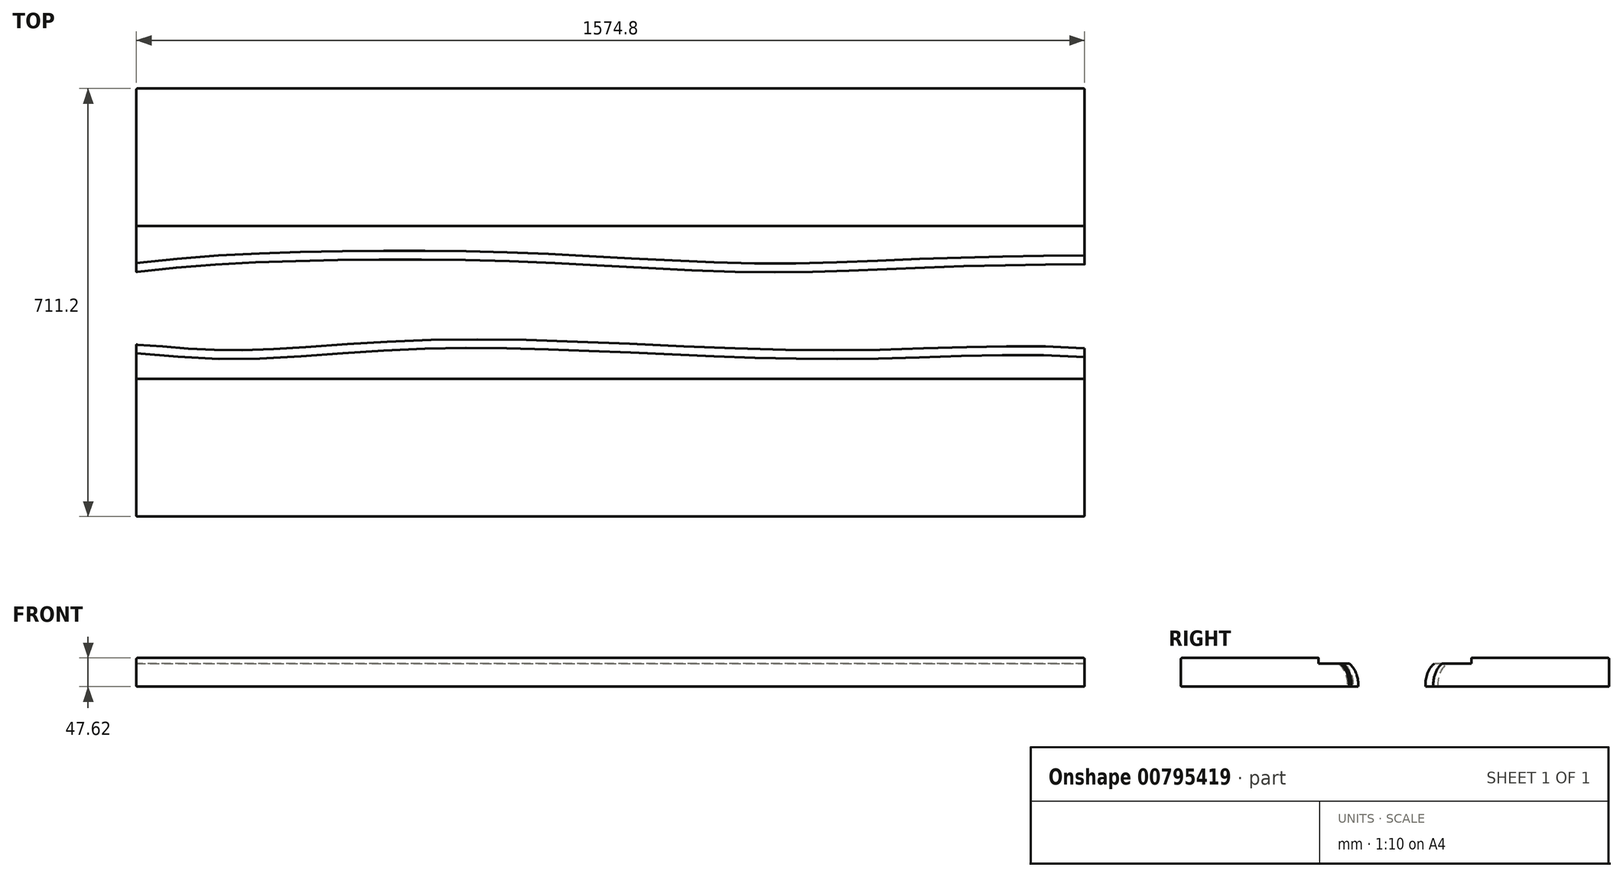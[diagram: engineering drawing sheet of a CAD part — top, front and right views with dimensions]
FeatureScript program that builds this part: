
annotation { "Feature Type Name" : "Feature", "Feature Type Description" : "" }
export const myFeature = defineFeature(function(context is Context, id is Id, definition is map)
    precondition{}
    {
        {
            var Q0;
            Q0=qCreatedBy(makeId("Top.planeOp"),FACE);
            var sketch = newSketch(context, id + "F0", { "sketchPlane" : qUnion([Q0])});
            skLineSegment(sketch, "E0.bottom", {"start": v(787.4, 355.6) * mm, "end": v(-787.4, 355.6) * mm});
            skLineSegment(sketch, "E0.top", {"start": v(787.4, -355.6) * mm, "end": v(-787.4, -355.6) * mm});
            skLineSegment(sketch, "E0.left", {"start": v(787.4, 355.6) * mm, "end": v(787.4, 63.5) * mm});
            skLineSegment(sketch, "E0.right", {"start": v(-787.4, 355.6) * mm, "end": v(-787.4, 50.8) * mm});
            skPoint(sketch, "E0.middle", {"position": v(0, 0) * mm});
            skFitSpline(sketch, "E1", {"points": [v(-787.4, 50.8) * mm, v(-491.45, 69.85) * mm, v(-145.69, 67.95) * mm, v(228.67, 50.8) * mm, v(493.84, 57.15) * mm, v(787.4, 63.5) * mm], "startDerivative": vector(1515.69, 196.01) * mm, "endDerivative": vector(1515.4, 0) * mm});
            skFitSpline(sketch, "E2", {"points": [v(-787.4, -69.85) * mm, v(-621.43, -79.38) * mm, v(-267.87, -61.35) * mm, v(361.25, -79.38) * mm, v(787.4, -76.2) * mm], "startDerivative": vector(997.51, -57.2) * mm, "endDerivative": vector(1451.8, -114.04) * mm});
            skLineSegment(sketch, "E3.trimOffspring", {"start": v(-787.4, -69.85) * mm, "end": v(-787.4, -355.6) * mm});
            skLineSegment(sketch, "E4.trimOffspring", {"start": v(787.4, -76.2) * mm, "end": v(787.4, -355.6) * mm});
            skSolve(sketch);
        }
        {
            var Q0;
            Q0 = qSketchRegion(id + "F0", true);
            extrude(context, id + "F1", {"entities" : qUnion([Q0]), "depth" : 47.62 * mm, "offsetDistance" : 25.4 * mm});
        }
        {
            var Q0;
            Q0=makeQuery(id+"F1.opExtrude","CAP_EDGE",EDGE,{"disambiguationData":[OSD([sQuery(id+"F0.wireOp",EDGE,"E2")])],"isStart":false});
            var Q1;
            Q1=makeQuery(id+"F1.opExtrude","CAP_EDGE",EDGE,{"disambiguationData":[OSD([sQuery(id+"F0.wireOp",EDGE,"E1")])],"isStart":false});
            fillet(context, id + "F2", {"entities" : qUnion([Q0, Q1]), "tangentPropagation" : true, "crossSection" : FilletCrossSection.CURVATURE, "radius" : 47.62 * mm, "magnitude" : 0.5, "defaultsChanged" : true, "vertexSettings" : []});
        }
        {
            var Q0;
            Q0=qCreatedBy(makeId("Right.planeOp"),FACE);
            var sketch = newSketch(context, id + "F3", { "sketchPlane" : qUnion([Q0])});
            skLineSegment(sketch, "E5.bottom", {"start": v(127, 38.1) * mm, "end": v(-127, 38.1) * mm});
            skLineSegment(sketch, "E5.top", {"start": v(127, 114.3) * mm, "end": v(-127, 114.3) * mm});
            skLineSegment(sketch, "E5.left", {"start": v(127, 38.1) * mm, "end": v(127, 114.3) * mm});
            skLineSegment(sketch, "E5.right", {"start": v(-127, 38.1) * mm, "end": v(-127, 114.3) * mm});
            skPoint(sketch, "E5.middle", {"position": v(0, 76.2) * mm});
            skSolve(sketch);
        }
        {
            var Q0;
            Q0 = qSketchRegion(id + "F3", true);
            extrude(context, id + "F4", {"entities" : qUnion([Q0]), "operationType" : NewBodyOperationType.REMOVE, "endBound" : BoundingType.THROUGH_ALL, "oppositeDirection" : true, "depth" : 25.4 * mm, "offsetDistance" : 25.4 * mm, "hasSecondDirection" : true, "secondDirectionBound" : SecondDirectionBoundingType.THROUGH_ALL, "secondDirectionOppositeDirection" : false, "secondDirectionDepth" : 25.4 * mm});
        }
        {
            var Q0;
            Q0=makeQuery(id+"F1.opExtrude","CAP_EDGE",EDGE,{"disambiguationData":[OSD([sQuery(id+"F0.wireOp",EDGE,"E0.right")])],"isStart":false});
            var Q1;
            Q1=makeQuery(id+"F1.opExtrude","CAP_EDGE",EDGE,{"disambiguationData":[OSD([sQuery(id+"F0.wireOp",EDGE,"E0.bottom")])],"isStart":false});
            var Q2;
            Q2=makeQuery(id+"F1.opExtrude","CAP_EDGE",EDGE,{"disambiguationData":[OSD([sQuery(id+"F0.wireOp",EDGE,"E3.trimOffspring")])],"isStart":false});
            var Q3;
            Q3=makeQuery(id+"F1.opExtrude","CAP_EDGE",EDGE,{"disambiguationData":[OSD([sQuery(id+"F0.wireOp",EDGE,"E0.top")])],"isStart":false});
            var Q4;
            Q4=makeQuery(id+"F1.opExtrude","CAP_EDGE",EDGE,{"disambiguationData":[OSD([sQuery(id+"F0.wireOp",EDGE,"E4.trimOffspring")])],"isStart":false});
            var Q5;
            Q5=makeQuery(id+"F1.opExtrude","CAP_EDGE",EDGE,{"disambiguationData":[OSD([sQuery(id+"F0.wireOp",EDGE,"E0.left")])],"isStart":false});
            var Q6;
            Q6=makeQuery(id+"F1.opExtrude","CAP_EDGE",EDGE,{"disambiguationData":[OSD([sQuery(id+"F0.wireOp",EDGE,"E0.left")])],"isStart":true});
            var Q7;
            Q7=makeQuery(id+"F1.opExtrude","CAP_EDGE",EDGE,{"disambiguationData":[OSD([sQuery(id+"F0.wireOp",EDGE,"E4.trimOffspring")])],"isStart":true});
            var Q8;
            Q8=makeQuery(id+"F1.opExtrude","CAP_EDGE",EDGE,{"disambiguationData":[OSD([sQuery(id+"F0.wireOp",EDGE,"E0.top")])],"isStart":true});
            var Q9;
            Q9=makeQuery(id+"F1.opExtrude","SWEPT_EDGE",EDGE,{"disambiguationData":[OSD([sQuery(id+"F0.wireOp",EDGE,"E0.top"),sQuery(id+"F0.wireOp",EDGE,"E4.trimOffspring")])]});
            var Q10;
            Q10=makeQuery(id+"F1.opExtrude","SWEPT_EDGE",EDGE,{"disambiguationData":[OSD([sQuery(id+"F0.wireOp",EDGE,"E0.bottom"),sQuery(id+"F0.wireOp",EDGE,"E0.left")])]});
            var Q11;
            Q11=makeQuery(id+"F1.opExtrude","SWEPT_EDGE",EDGE,{"disambiguationData":[OSD([sQuery(id+"F0.wireOp",EDGE,"E0.top"),sQuery(id+"F0.wireOp",EDGE,"E3.trimOffspring")])]});
            var Q12;
            Q12=makeQuery(id+"F1.opExtrude","CAP_EDGE",EDGE,{"disambiguationData":[OSD([sQuery(id+"F0.wireOp",EDGE,"E0.bottom")])],"isStart":true});
            var Q13;
            Q13=makeQuery(id+"F1.opExtrude","CAP_EDGE",EDGE,{"disambiguationData":[OSD([sQuery(id+"F0.wireOp",EDGE,"E0.right")])],"isStart":true});
            var Q14;
            Q14=makeQuery(id+"F1.opExtrude","CAP_EDGE",EDGE,{"disambiguationData":[OSD([sQuery(id+"F0.wireOp",EDGE,"E3.trimOffspring")])],"isStart":true});
            var Q15;
            Q15=makeQuery(id+"F1.opExtrude","SWEPT_EDGE",EDGE,{"disambiguationData":[OSD([sQuery(id+"F0.wireOp",EDGE,"E0.bottom"),sQuery(id+"F0.wireOp",EDGE,"E0.right")])]});
            fillet(context, id + "F5", {"entities" : qUnion([Q0, Q1, Q2, Q3, Q4, Q5, Q6, Q7, Q8, Q9, Q10, Q11, Q12, Q13, Q14, Q15]), "tangentPropagation" : true, "radius" : 1.59 * mm, "defaultsChanged" : true, "vertexSettings" : [], "allowEdgeOverflow" : false});
        }
    });
